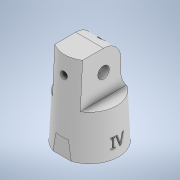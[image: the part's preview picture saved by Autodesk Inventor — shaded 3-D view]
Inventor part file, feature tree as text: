
AUTODESK INVENTOR PART (.ipt)
format: ipt  version: 2021 (Build 250183000, 183)  size: 552,448 bytes
history: native  units: mm
features: sketch x9, other x7, extrude x6, hole x2, fillet x2, plane x2, chamfer x1
ambient origin geometry x8: Origin, YZ Plane, XZ Plane, XY Plane, X Axis, Y Axis, Z Axis, Center Point
bodies: Volumenkörper1 (feature_tree), Volumenkörper2 (feature_tree), Volumenkörper3 (feature_tree), Volumenkörper5 (feature_tree), Volumenkörper6 (feature_tree), Volumenkörper7 (feature_tree)
feature tree (29):
  extrude  "Extrusion1"  Depth=20.0mm
  other  "Flächenverjüngung1"
  extrude  "Extrusion2"  Depth=30.0mm TaperAngle=0.0deg
  other  "Kombinieren1"
  hole  "Bohrung1"  [1 undecoded]
  extrude  "Extrusion3"  Depth=30.0mm TaperAngle=0.0deg
  fillet  "Rundung5"  Radius=4.8mm
  other  "Kombinieren3"
  fillet  "Rundung6"  Radius=15.0mm
  extrude  "Extrusion5"  Depth=6.0mm
  other  "Kombinieren6"
  plane  "Arbeitsebene1"
  extrude  "Extrusion6"  Depth=6.0mm
  other  "Kombinieren7"
  hole  "Bohrung2"  [1 undecoded]
  extrude  "Extrusion8"  [1 undecoded]
  other  "Kombinieren8"
  plane  "Arbeitsebene3"
  other  "Prägen1"
  chamfer  "Fase1"  Distance=2.4mm
  sketch  "Skizze1"  dims[d0=30.0mm d1=0.0mm d2=20.0mm]
  sketch  "Skizze2"  dims[d3=0.0mm d7=30.0mm d8=0.0mm]
  sketch  "Skizze3"  dims[d9=4.0mm d10=6.0mm d11=4.0mm d12=2.0mm d13=90.0deg d14=8.0mm d15=20.594885mm d16=0.0mm]
  sketch  "Skizze4"  dims[d17=5.0mm d19=30.0mm d20=0.0mm d25=4.8mm d27=15.0mm]
  sketch  "Skizze6"  dims[d28=7.25mm d29=6.0mm]
  sketch  "Skizze7"  dims[d32=5.0mm d33=6.0mm]
  sketch  "Skizze8"  dims[d42=6.0mm d43=40.0mm d44=0.0mm]
  sketch  "Skizze10"  dims[d45=9.5mm d46=-0.436332mm]
  sketch  "Skizze11"  dims[d47=3.5mm d49=2.4mm d51=24.0mm d52=10.0mm d53=0.0mm d54=2.0mm d55=6.0mm d56=4.0mm d57=2.0mm d58=90.0deg d59=8.0mm d60=20.594885mm d61=0.0mm d62=4.0mm d64=4.8mm d73=0.0mm d74=2.5mm d75=2.5mm d76=0.0mm d77=3.0mm d78=3.0mm d79=10.0mm d80=0.0mm d82=9.0mm d83=3.5mm d84=5.5mm d85=2.5mm d86=3.0mm d87=0.5mm d88=0.0mm d90=1.2mm d91=2.2mm d92=45.0deg d93=4.0mm d18=0.0625mm d34=0.5mm d35=0.872665mm]
note: 3 required parameter values undecoded (feature->parameter linkage not recoverable at this tier; creation-order binding heuristic only, values carry confidence <= 0.55)
